# Revit family: Reece_Shower_Posh_Solus MK3_Grab Rail Shower_Conversion Kit
name_source: partatom
category: Plumbing Fixtures
revit_build: Autodesk Revit 2018 (Build: 20180329_1100(x64)
units: mm (PartAtom-declared; Revit-internal decimal feet)

## family parameters
Always vertical = Yes
Cut with Voids When Loaded = Yes
Part Type = Normal
Room Calculation Point = Yes
Round Connector Dimension = Use Diameter
Shared = Yes
Work Plane-Based = Yes

## types (1)
- Chrome
    Default Elevation = 0 mm  [stored 0 ft]
    Description = Posh Solus MK3 Grab Rail Shower Conversion Kit 1 Function Chrome (4 Star)
    Disclaimer = THIS FILE IS THE PROPERTY OF THE REECE GROUP. IT MAY NOT BE REPRODUCED, REVERSE-ENGINEERED OR MODIFIED. ANY REPUBLICATION, TRANSMISSION OR DISTRIBUTION FOR THE PURPOSE OF COMMERCIALLY EXPLOITING THE FILES IS PROHIBITED.
    Keynote = Product #2213369, Reece_Shower_Posh_Solus MK3_Grab Rail Shower_Conversion Kit - Chrome
    Manufacturer = Posh
    Model = Solus MK3
    Reece_Detail_Additional = With Wall Bracket
    Reece_Detail_Connector = 1 Function
    Reece_Detail_Disclaimer = THIS FILE IS THE PROPERTY OF THE REECE GROUP. IT MAY NOT BE REPRODUCED, REVERSE-ENGINEERED OR MODIFIED. ANY REPUBLICATION, TRANSMISSION OR DISTRIBUTION FOR THE PURPOSE OF COMMERCIALLY EXPLOITING THE FILES IS PROHIBITED.
    Reece_Material_Colour = Reece_Plastic_ABS
    Reece_Material_Main = Reece_Brass_Chrome
    Reece_Material_Secondary = Reece_Plastic_White
    Reece_Overall_Diameter = 100 mm  [stored 0.328084 ft]
    Reece_Overall_Width = 108 mm
    Reece_Product_Brand = Posh
    Reece_Product_Description = Posh Solus MK3 Grab Single Rail Shower Conversion Kit 1 Function with Wall Water Inlet Chrome (4 Star)
    Reece_Product_Mount = Wall Mounted
    Reece_Product_Number = 2213369
    Reece_Product_Sub Brand = Solus MK3
    Reece_Product_Type = Shower
    Reece_Product_Web Page = https://www.reece.com.au
    Reece_Shower_Inlet = 12 mm  [stored 0.0393701 ft]
    Type Comments = Shower
    URL = https://www.reece.com.au

note: [stored X ft] marks values corroborated as IEEE doubles in the binary element streams (Revit-internal decimal feet)

## geometry (parser evidence)
native form markers: Sweep x6
no freeform markers — native parametric forms only
